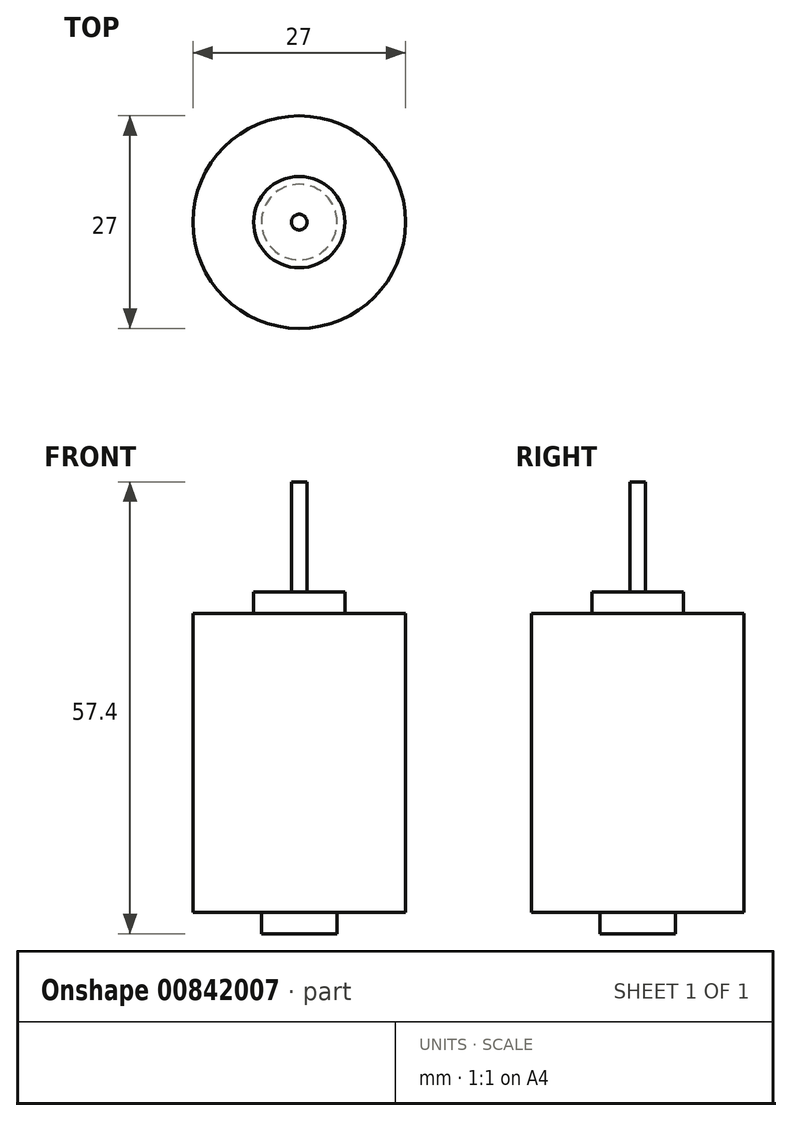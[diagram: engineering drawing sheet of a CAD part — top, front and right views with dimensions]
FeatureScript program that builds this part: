
annotation { "Feature Type Name" : "Feature", "Feature Type Description" : "" }
export const myFeature = defineFeature(function(context is Context, id is Id, definition is map)
    precondition{}
    {
        {
            var Q0;
            Q0=qCreatedBy(makeId("Right.planeOp"),FACE);
            var sketch = newSketch(context, id + "F0", { "sketchPlane" : qUnion([Q0])});
            skLineSegment(sketch, "E0", {"start": v(-30.55, 5.8) * mm, "end": v(-30.55, -51.58) * mm});
            skLineSegment(sketch, "E1", {"start": v(-30.55, -51.58) * mm, "end": v(-25.75, -51.58) * mm});
            skLineSegment(sketch, "E2", {"start": v(-25.75, -51.58) * mm, "end": v(-25.75, -48.88) * mm});
            skLineSegment(sketch, "E3", {"start": v(-25.75, -48.88) * mm, "end": v(-17.05, -48.88) * mm});
            skLineSegment(sketch, "E4", {"start": v(-17.05, -48.88) * mm, "end": v(-17.05, -10.88) * mm});
            skLineSegment(sketch, "E5", {"start": v(-17.05, -10.88) * mm, "end": v(-24.75, -10.88) * mm});
            skLineSegment(sketch, "E6", {"start": v(-24.75, -10.88) * mm, "end": v(-24.75, -8.18) * mm});
            skLineSegment(sketch, "E7", {"start": v(-24.75, -8.18) * mm, "end": v(-29.55, -8.18) * mm});
            skLineSegment(sketch, "E8", {"start": v(-29.55, -8.18) * mm, "end": v(-29.55, 5.82) * mm});
            skLineSegment(sketch, "E9", {"start": v(-29.55, 5.82) * mm, "end": v(-30.55, 5.82) * mm});
            skLineSegment(sketch, "E10", {"start": v(-30.55, 5.82) * mm, "end": v(-30.55, 5.8) * mm});
            skSolve(sketch);
        }
        {
            var Q0;
            Q0=makeQuery(id+"F0.imprint","IMPRINT",FACE,{"disambiguationData":[TD([[makeQuery(id+"F0.imprint","IMPRINT",EDGE,{"derivedFrom":sQuery(id+"F0.wireOp",EDGE,"E0")}),1.0]])]});
            var Q1;
            Q1=sQuery(id+"F0.wireOp",EDGE,"E0");
            revolve(context, id + "F1", {"surfaceOperationType" : NewSurfaceOperationType.NEW, "entities" : qUnion([Q0]), "axis" : qUnion([Q1]), "revolveType" : RevolveType.FULL});
        }
    });
